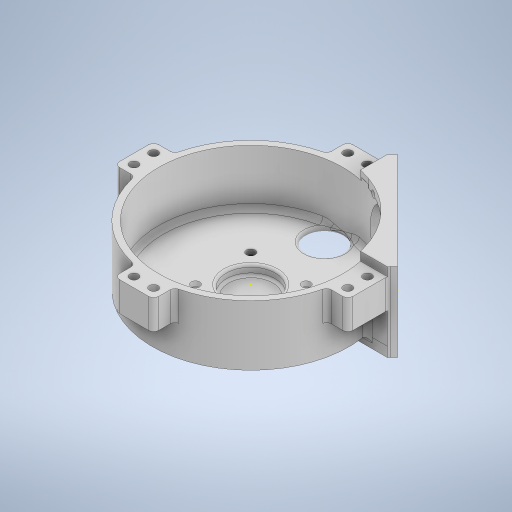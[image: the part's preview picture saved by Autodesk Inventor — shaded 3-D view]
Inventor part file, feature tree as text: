
AUTODESK INVENTOR PART (.ipt)
format: ipt  version: 2023 (Build 270158000, 158)  size: 783,360 bytes
history: native  units: in
note: dims shown in document units (in); Inventor stores cm internally (conversion verified against a paired STEP export)
features: sketch x25, extrude x20, fillet x11, hole x3
ambient origin geometry x8: Origin, YZ Plane, XZ Plane, XY Plane, X Axis, Y Axis, Z Axis, Center Point
bodies: Solid1 (feature_tree)
feature tree (59):
  extrude  "Extrusion1"  Depth=1.375in TaperAngle=0.0deg
  extrude  "Extrusion2"  Depth=1.275in TaperAngle=0.0deg
  extrude  "Extrusion3"  Depth=1.125in TaperAngle=0.0deg
  hole  "Hole1"  [1 undecoded]
  extrude  "Extrusion4"  Depth=0.4in
  extrude  "Extrusion5"  Depth=0.4in
  hole  "Hole2"  [1 undecoded]
  extrude  "Extrusion6"  Depth=0.4in
  sketch  "Sketch10"  dims[d26=0.8in d27=0.4in]
  extrude  "Extrusion7"  Depth=0.4in
  extrude  "Extrusion8"  Depth=0.8in
  extrude  "Extrusion9"  Depth=0.4in
  extrude  "Extrusion18"  Depth=0.75in TaperAngle=0.0deg
  extrude  "Extrusion19"  Depth=0.2in
  extrude  "Extrusion20"  Depth=0.2in
  extrude  "Extrusion21"  Depth=0.2in
  extrude  "Extrusion22"  Depth=0.2in
  extrude  "Extrusion23"  Depth=0.2in
  sketch  "Sketch34"  dims[d125=0.3in d126=0.3in]
  hole  "Hole6"  [1 undecoded]
  extrude  "Extrusion24"  Depth=0.2in TaperAngle=0.0deg
  fillet  "Fillet1"  Radius=2.0in
  fillet  "Fillet2"  Radius=0.3in
  fillet  "Fillet3"  Radius=0.3in
  fillet  "Fillet4"  Radius=0.3in
  fillet  "Fillet5"  Radius=0.3in
  fillet  "Fillet6"  Radius=0.1in
  fillet  "Fillet7"  Radius=0.1in
  fillet  "Fillet8"  Radius=0.175in
  fillet  "Fillet9"  Radius=0.2in
  fillet  "Fillet10"  Radius=1.0875in
  fillet  "Fillet11"  Radius=1.425in
  extrude  "Extrusion11"  Depth=0.5in
  extrude  "Extrusion13"  Depth=0.5in
  extrude  "Extrusion14"  Depth=0.3in
  extrude  "Extrusion16"  Depth=0.3in
  sketch  "Sketch1"  dims[d0=4.0in d1=1.375in d2=0.0in]
  sketch  "Sketch2"  dims[d3=3.75in d4=1.275in d5=0.0in]
  sketch  "Sketch3"  dims[d6=1.0in d7=1.125in d8=0.0in]
  sketch  "Sketch4"  dims[d9=1.125in d10=1.125in]
  sketch  "Sketch5"  dims[d11=0.177in d12=0.75in d13=0.332in d14=0.25in d15=0.5635in d16=1.0in d17=0.8108in d18=0.4in]
  sketch  "Sketch6"  dims[d19=0.5in d20=0.4in]
  sketch  "Sketch7"  dims[d21=0.5in d22=0.75in d23=0.0in]
  sketch  "Sketch8"  dims[d24=0.5in d25=0.4in]
  sketch  "Sketch11"  dims[d28=0.5in d29=0.8in]
  sketch  "Sketch12"  dims[d30=0.5in d31=0.4in]
  sketch  "Sketch13"  dims[d32=0.8in d33=0.75in d34=0.0in]
  sketch  "Sketch17"  dims[d35=0.2in d36=0.2in]
  sketch  "Sketch19"  dims[d37=0.4in d38=0.2in]
  sketch  "Sketch20"  dims[d39=0.2in d40=0.4in]
  sketch  "Sketch23"  dims[d41=0.2in d42=0.2in]
  sketch  "Sketch26"  dims[d43=0.2in d44=0.2in]
  sketch  "Sketch27"  dims[d45=0.4in]
  sketch  "Sketch28"  dims[d46=0.177in d47=0.75in d48=0.375in d49=0.25in d50=0.5635in d51=0.75in d52=0.8108in d53=1.5in]
  sketch  "Sketch30"  dims[d54=0.75in d55=0.0in d66=0.15in d67=0.0in d68=2.0in d69=0.3in d70=0.3in d71=0.3in d72=0.3in d73=0.1in d74=0.0in d75=0.1in d76=0.0in d79=0.175in d80=0.0in d84=0.2in d85=0.0in d86=1.0875in d87=0.0in d101=1.425in d102=0.0in]
  sketch  "Sketch32"  dims[d105=0.3in d106=0.0in d122=0.5in]
  sketch  "Sketch33"  dims[d123=0.5in d124=0.5in]
  sketch  "Sketch35"  dims[d127=0.3in d128=0.3in]
  sketch  "Sketch36"  dims[d129=0.175in d130=1.225in d131=0.0in d132=0.0in d133=0.0625in d134=1.125in d135=0.0in d136=0.0in d137=0.15in d138=1.6in d139=0.0in d140=0.375in d141=0.0in d142=0.2in d143=0.0in d144=0.3in d145=0.2in d146=0.0in d147=0.8in d148=1.275in d149=1.275in d150=0.126in d151=0.75in d152=0.248in d153=0.25in d154=90.0deg d155=0.5in d156=0.8108in d157=1.5in d158=0.4in d159=0.0in d160=0.25in d161=0.25in d162=0.25in d163=0.1in d164=0.1in d165=0.1in d166=0.1in d167=0.05in d168=0.05in d169=0.1in d170=0.1in d81=0.5in d82=0.0344in]
note: 3 required parameter values undecoded (feature->parameter linkage not recoverable at this tier; creation-order binding heuristic only, values carry confidence <= 0.55)
